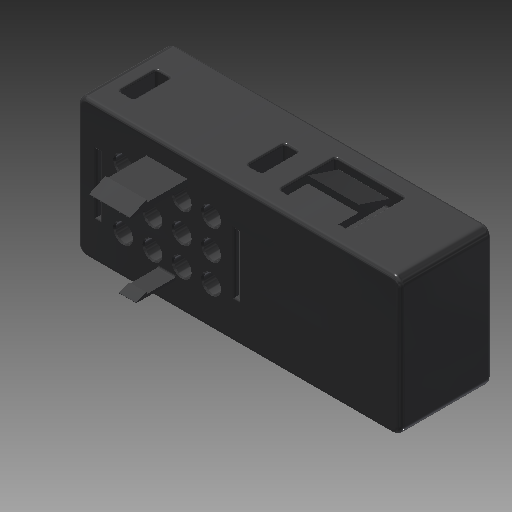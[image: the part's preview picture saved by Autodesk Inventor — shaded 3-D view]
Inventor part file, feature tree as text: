
AUTODESK INVENTOR PART (.ipt)
format: ipt  version: 2019 (Build 230136000, 136)  size: 555,008 bytes
history: native  units: mm
features: sketch x23, extrude x12, fillet x12, projected_geometry x7, plane x3, mirror x3, chamfer x1, pattern_linear x1
ambient origin geometry x8: Origin, YZ Plane, XZ Plane, XY Plane, X Axis, Y Axis, Z Axis, Center Point
bodies: Solid1 (feature_tree)
feature tree (62):
  extrude  "Extrusion1"  Depth=70.0mm
  extrude  "Extrusion2"  Depth=15.0mm
  chamfer  "Chamfer1"  Distance=20.0mm
  extrude  "Extrusion3"  Depth=6.35mm
  extrude  "Extrusion4"  Depth=6.35mm TaperAngle=0.0deg
  fillet  "Fillet1"  Radius=0.0762mm
  pattern_linear  "Rectangular Pattern1"  Count1=4 Spacing1=6.35mm
  plane  "Work Plane1"
  extrude  "Extrusion5"  [1 undecoded]
  fillet  "Fillet2"  Radius=9.525mm
  fillet  "Fillet3"  Radius=1.27mm
  extrude  "Extrusion6"  Depth=4.0mm
  fillet  "Fillet4"  Radius=4.363323mm
  fillet  "Fillet5"  Radius=8.89mm
  extrude  "Extrusion7"  Depth=0.5mm
  extrude  "Extrusion8"  Depth=8.89mm
  fillet  "Fillet6"  Radius=6.35mm
  fillet  "Fillet7"  Radius=2.5mm
  fillet  "Fillet8"  Radius=3.490659mm
  mirror  "Mirror1"
  extrude  "Extrusion9"  Depth=0.05mm
  extrude  "Extrusion10"  Depth=6.35mm
  mirror  "Mirror2"
  sketch  "Sketch11"  dims[d25=30.0mm d27=6.35mm d28=-15.475mm d29=9.525mm d30=1.27mm]
  sketch  "Sketch12"  dims[d31=8.89mm d32=4.0mm d33=4.363323mm d34=8.89mm d35=0.0mm]
  sketch  "Sketch13"  dims[d36=0.127mm d37=0.5mm]
  sketch  "Sketch14"  dims[d42=0.5588mm d43=8.89mm d44=6.35mm d45=2.5mm d46=3.490659mm]
  sketch  "Sketch15"  dims[d47=3.81mm d48=0.0mm d49=0.05mm]
  sketch  "Sketch16"  dims[d50=0.5mm d51=6.35mm d52=12.7mm d53=0.762mm d54=14.605mm]
  sketch  "Sketch17"  dims[d55=10.0mm d56=0.0mm d57=5.08mm]
  sketch  "Sketch18"  dims[d58=8.0mm d59=3.0mm d61=15.0mm d62=0.0mm]
  sketch  "Sketch19"  dims[d63=0.5mm]
  sketch  "Sketch20"  dims[d64=0.5mm]
  sketch  "Sketch21"  dims[d65=0.5mm]
  fillet  "Fillet9"  Radius=12.7mm
  fillet  "Fillet10"  Radius=0.762mm
  fillet  "Fillet11"  Radius=14.605mm
  extrude  "Extrusion11"  Depth=5.08mm
  plane  "Work Plane2"
  extrude  "Extrusion12"  Depth=3.0mm
  fillet  "Fillet13"  Radius=15.0mm
  mirror  "Mirror3"
  sketch  "Sketch1"  dims[d0=70.0mm d1=35.0mm]
  sketch  "Sketch2"  dims[d2=30.0mm d3=15.0mm d4=20.0mm d5=0.0mm]
  sketch  "Sketch3"  dims[d6=3.81mm d7=6.35mm]
  sketch  "Sketch4"  dims[d8=25.0mm d9=6.35mm d10=0.0mm]
  sketch  "Sketch5"  dims[d11=0.254mm d12=2.0mm d13=45.0deg d14=0.0762mm]
  projected_geometry  "Projected Loop1"
  sketch  "Sketch6"  dims[d15=1.27mm]
  projected_geometry  "Projected Loop2"
  sketch  "Sketch7"  dims[d16=3.81mm d17=0.0mm]
  sketch  "Sketch8"  dims[d18=2.54mm]
  projected_geometry  "Projected Loop3"
  sketch  "Sketch9"  dims[d19=0.254mm d20=0.0mm]
  sketch  "Sketch10"  dims[d21=0.127mm d22=40.0mm d24=6.35mm]
  sketch  "Sketch22"  dims[d66=10.0mm]
  projected_geometry  "Projected Loop4"
  sketch  "Sketch23"  dims[d67=35.0mm d68=17.5mm d69=5.0mm d70=0.0mm d71=0.5mm d72=7.5mm d73=3.0mm d74=0.0mm d75=2.0mm d76=1.0mm d77=1.0mm d78=5.0mm d79=15.0mm d80=4.0mm d81=12.0mm d82=4.0mm d83=0.0mm d84=8.0mm d85=1.5mm d86=1.5mm d88=9.0mm d89=11.0mm d90=0.0mm d92=0.5mm d93=0.4mm]
  projected_geometry  "Projected Loop5"
  projected_geometry  "Projected Loop6"
  projected_geometry  "Projected Loop7"
  plane  "Work Plane3"
note: 1 required parameter value undecoded (feature->parameter linkage not recoverable at this tier; creation-order binding heuristic only, values carry confidence <= 0.55)
